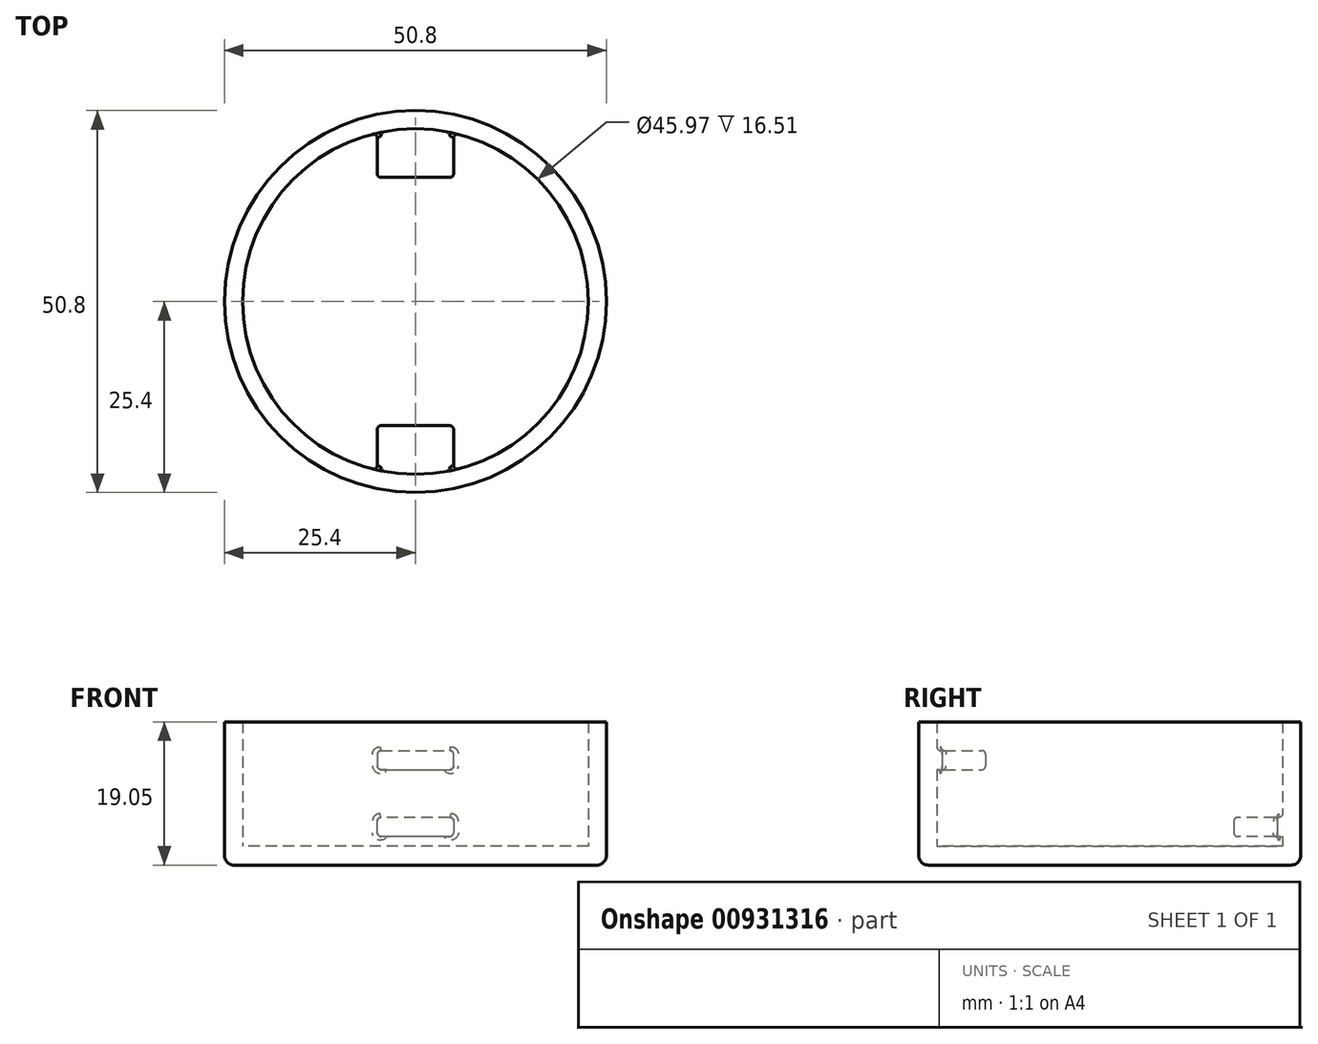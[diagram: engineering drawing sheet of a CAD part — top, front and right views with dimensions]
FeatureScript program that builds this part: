
annotation { "Feature Type Name" : "Feature", "Feature Type Description" : "" }
export const myFeature = defineFeature(function(context is Context, id is Id, definition is map)
    precondition{}
    {
        {
            var Q0;
            Q0=qCreatedBy(makeId("Top.planeOp"),FACE);
            var sketch = newSketch(context, id + "F0", { "sketchPlane" : qUnion([Q0])});
            skCircle(sketch, "E0", {"center": v(0, 0) * mm, "radius": 25.4 * mm});
            skSolve(sketch);
        }
        {
            var Q0;
            Q0 = qSketchRegion(id + "F0", true);
            extrude(context, id + "F1", {"entities" : qUnion([Q0]), "depth" : 2.54 * mm, "offsetDistance" : 25.4 * mm});
        }
        {
            var Q0;
            Q0=makeQuery(id+"F1.opExtrude","CAP_FACE",FACE,{"disambiguationData":[OSD([sQuery(id+"F0.wireOp",EDGE,"E0")])],"isStart":false});
            var sketch = newSketch(context, id + "F2", { "sketchPlane" : qUnion([Q0])});
            skCircle(sketch, "E1", {"center": v(0, 0) * mm, "radius": 22.99 * mm});
            skCircle(sketch, "E2", {"center": v(0, 0) * mm, "radius": 25.4 * mm});
            skSolve(sketch);
        }
        {
            var Q0;
            Q0 = qSketchRegion(id + "F2", true);
            extrude(context, id + "F3", {"entities" : qUnion([Q0]), "operationType" : NewBodyOperationType.ADD, "depth" : 16.5 * mm, "offsetDistance" : 25.4 * mm});
        }
        {
            var Q0;
            Q0=qCreatedBy(makeId("Front.planeOp"),FACE);
            cPlane(context, id + "F4", {"entities" : qUnion([Q0]), "cplaneType" : CPlaneType.OFFSET, "offset" : 16.5 * mm, "width" : 152.4 * mm, "height" : 152.4 * mm});
        }
        {
            var Q0;
            Q0=qCreatedBy(makeId("Front.planeOp"),FACE);
            cPlane(context, id + "F5", {"entities" : qUnion([Q0]), "cplaneType" : CPlaneType.OFFSET, "offset" : 16.5 * mm, "oppositeDirection" : true, "width" : 152.4 * mm, "height" : 152.4 * mm});
        }
        {
            var Q0;
            Q0=qCreatedBy(id+"F4.planeOp",FACE);
            var sketch = newSketch(context, id + "F6", { "sketchPlane" : qUnion([Q0])});
            skLineSegment(sketch, "E3.bottom", {"start": v(-5.08, 15.24) * mm, "end": v(5.08, 15.24) * mm});
            skLineSegment(sketch, "E3.top", {"start": v(-5.08, 12.7) * mm, "end": v(5.08, 12.7) * mm});
            skLineSegment(sketch, "E3.left", {"start": v(-5.08, 15.24) * mm, "end": v(-5.08, 12.7) * mm});
            skLineSegment(sketch, "E3.right", {"start": v(5.08, 15.24) * mm, "end": v(5.08, 12.7) * mm});
            skSolve(sketch);
        }
        {
            var Q0;
            Q0 = qSketchRegion(id + "F6", true);
            extrude(context, id + "F7", {"entities" : qUnion([Q0]), "operationType" : NewBodyOperationType.ADD, "endBound" : BoundingType.UP_TO_NEXT, "depth" : 25.4 * mm, "offsetDistance" : 25.4 * mm});
        }
        {
            var Q0;
            Q0=qCreatedBy(id+"F5.planeOp",FACE);
            var sketch = newSketch(context, id + "F8", { "sketchPlane" : qUnion([Q0])});
            skLineSegment(sketch, "E4.bottom", {"start": v(5.08, 6.35) * mm, "end": v(-5.08, 6.35) * mm});
            skLineSegment(sketch, "E4.top", {"start": v(5.08, 3.81) * mm, "end": v(-5.08, 3.8) * mm});
            skLineSegment(sketch, "E4.left", {"start": v(5.08, 6.35) * mm, "end": v(5.08, 3.81) * mm});
            skLineSegment(sketch, "E4.right", {"start": v(-5.08, 6.35) * mm, "end": v(-5.08, 3.8) * mm});
            skSolve(sketch);
        }
        {
            var Q0;
            Q0 = qSketchRegion(id + "F8", true);
            extrude(context, id + "F9", {"entities" : qUnion([Q0]), "operationType" : NewBodyOperationType.ADD, "endBound" : BoundingType.UP_TO_NEXT, "oppositeDirection" : true, "depth" : 25.4 * mm, "offsetDistance" : 25.4 * mm});
        }
        {
            var Q0;
            Q0=makeQuery(id+"F1.opExtrude","CAP_EDGE",EDGE,{"disambiguationData":[OSD([sQuery(id+"F0.wireOp",EDGE,"E0")])],"isStart":true});
            fillet(context, id + "F10", {"entities" : qUnion([Q0]), "radius" : 1.27 * mm, "tangentPropagation" : true, "allowEdgeOverflow" : false});
        }
        {
            var Q0;
            Q0=makeQuery(id+"F7.opExtrude","SWEPT_FACE",FACE,{"disambiguationData":[OSD([sQuery(id+"F6.wireOp",EDGE,"E3.bottom")])]});
            var Q1;
            Q1=makeQuery(id+"F7.opExtrude","SWEPT_FACE",FACE,{"disambiguationData":[OSD([sQuery(id+"F6.wireOp",EDGE,"E3.left")])]});
            var Q2;
            Q2=makeQuery(id+"F7.opExtrude","SWEPT_FACE",FACE,{"disambiguationData":[OSD([sQuery(id+"F6.wireOp",EDGE,"E3.right")])]});
            var Q3;
            Q3=makeQuery(id+"F7.opExtrude","CAP_FACE",FACE,{"disambiguationData":[OSD([sQuery(id+"F6.wireOp",EDGE,"E3.bottom"),sQuery(id+"F6.wireOp",EDGE,"E3.top"),sQuery(id+"F6.wireOp",EDGE,"E3.left"),sQuery(id+"F6.wireOp",EDGE,"E3.right")])],"isStart":true});
            var Q4;
            Q4=makeQuery(id+"F10.opFillet","BLEND_FACE",FACE,{"disambiguationData":[OSD([sQuery(id+"F0.wireOp",EDGE,"E0")])]});
            var Q5;
            Q5=makeQuery(id+"F9.opExtrude","SWEPT_FACE",FACE,{"disambiguationData":[OSD([sQuery(id+"F8.wireOp",EDGE,"E4.bottom")])]});
            var Q6;
            Q6=makeQuery(id+"F9.opExtrude","CAP_FACE",FACE,{"disambiguationData":[OSD([sQuery(id+"F8.wireOp",EDGE,"E4.bottom"),sQuery(id+"F8.wireOp",EDGE,"E4.top"),sQuery(id+"F8.wireOp",EDGE,"E4.left"),sQuery(id+"F8.wireOp",EDGE,"E4.right")])],"isStart":true});
            var Q7;
            Q7=makeQuery(id+"F9.opExtrude","SWEPT_FACE",FACE,{"disambiguationData":[OSD([sQuery(id+"F8.wireOp",EDGE,"E4.left")])]});
            var Q8;
            Q8=makeQuery(id+"F9.opExtrude","SWEPT_FACE",FACE,{"disambiguationData":[OSD([sQuery(id+"F8.wireOp",EDGE,"E4.right")])]});
            fillet(context, id + "F11", {"entities" : qUnion([Q0, Q1, Q2, Q3, Q4, Q5, Q6, Q7, Q8]), "radius" : 0.5 * mm, "tangentPropagation" : true, "allowEdgeOverflow" : false});
        }
    });
